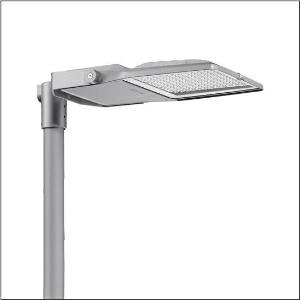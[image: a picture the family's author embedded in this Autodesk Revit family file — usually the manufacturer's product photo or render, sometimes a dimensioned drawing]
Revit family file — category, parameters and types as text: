
# Revit family: floodlight_fl_21_iq_midi___pl52_5xa7782f2d3a_028a
name_source: partatom
category: Lighting Fixtures
units: mm (PartAtom-declared; Revit-internal decimal feet)

## family parameters
Cut with Voids When Loaded = No
Host = Face
Light Source = No
Part Type = Normal
Room Calculation Point = No
Round Connector Dimension = Use Diameter
Shared = No

## types (1)
- --- (1 x LED, 35760 lm, 270.2 W, 3000K)
    Apparent Load = 270 VA
    CIE Flux Codes = 26 60 98 100 100
    Color Rendering = 70
    Color Temperature = 3000K
    Default Elevation = 1800 mm
    Description = Floodlight FL 21 iQ midi, floodlight, primary light control with lens, of PMMA, primary optical cover: protective disc, of toughened safety glass, transparent, light distribution: PL52, light emission: direct distribution, installation type: surface-mounted, lamps: LED, High Power LED, rated values: 35.760lm | 270,2W | 132,3lm/W (begin service life); end service life: 35.760lm | 286,6W; at 50% lumin. flux: 17.880lm | 117,4W | 152,3lm/W, colour temperature: 3000K, colour rendering: CRI > 70, light colour: 730, light setting 1 begin service life: 100% | 35.760lm | 270,2W | 132,3lm/W | 3.000K, light setting 1 end service life: 286,6W, further light settings possible, control: optimised constant luminous flux control (CLO 2.0), Desk-Remote (wireless, voltage-free reading and setting of iQ features in the workshop via application-optimized NFC function/RFID function), Smart-Wire, Night-Set, Temp-Guard, Auto-Match, Street-Remote, pre-setting: linear dimming characteristic, with terminal, 6-pole, mains connection: 220..240V, AC, 50/60Hz, luminaire housing, of diecast aluminium, powder-coated, SITECO metallic grey (DB 702S), corrosivity category C5 mid according to DIN EN ISO 12944suitable for swimming poolschlorine-resistant, sealing non-destructively replaceable, please order mast flange separately, mast bracket, of steel, galvanised, powder-coated, SITECO metallic grey (DB 702S), protection rating (complete): IP66, insulation class (complete): insulation class II (safety insulation), certification: CE, ENEC, VDE, protection symbol: D, impact resistance: IK08, permissible operating ambient temperature: -40..+40°C, permissible operating ambient temperature for outdoor applications: -40..+50°C, standard: DIN EN 12944, LABS conformity tested according to VDMA 24364:2018-05, packaging unit: 1 piece

Light Distribution: PL52
    Height = 76 mm
    Lamp = 1 x LED
    Lamp Light Flux = 35760 lm
    Lamp Power = 270.2 W
    Lamp count = 1
    Length = 657 mm
    Luminous efficacy = 132 lm/W
    Manufacturer = Siteco
    ModVariant = No
    Model = 5XA7782F2D3A
    Mounting Place = Pole
    Mounting Type = Pole annexe
    Number of Poles = 1
    OnlyDefault = Yes
    Power Factor = 1
    Product Name = Floodlight FL 21 iQ midi | PL52
    Product group = floodlight | pylon annexe
    ProductGroupID = 6201
    Protection Class = Protection class II
    Protection Degree = IP 66
    RLX_Detail_Level = 1
    RLX_Emergency_Light_Flux = 0 lm
    RLX_Emergency_Type = 0
    RLX_Emergency_Type_DB = No
    RlxData = <blob elided: 154385 chars, md5=ce418f70>
    Socket = socket
    Standby Power = 0 W
    System Light Flux = 35760 lm
    System Power = 270 W
    Type Comments = factory setting: luminous flux: 100 % | dim-lin: 254 | 620 mA
    Type Image = l_1007123.jpg
    URL = http://relux.com
    VarID = @adj_107137
    Voltage = 0 V
    Weight = 0.00 kg
    Width = 442 mm

## geometry (parser evidence)
native form markers: Blend x4, Sweep x13
no freeform markers — native parametric forms only
